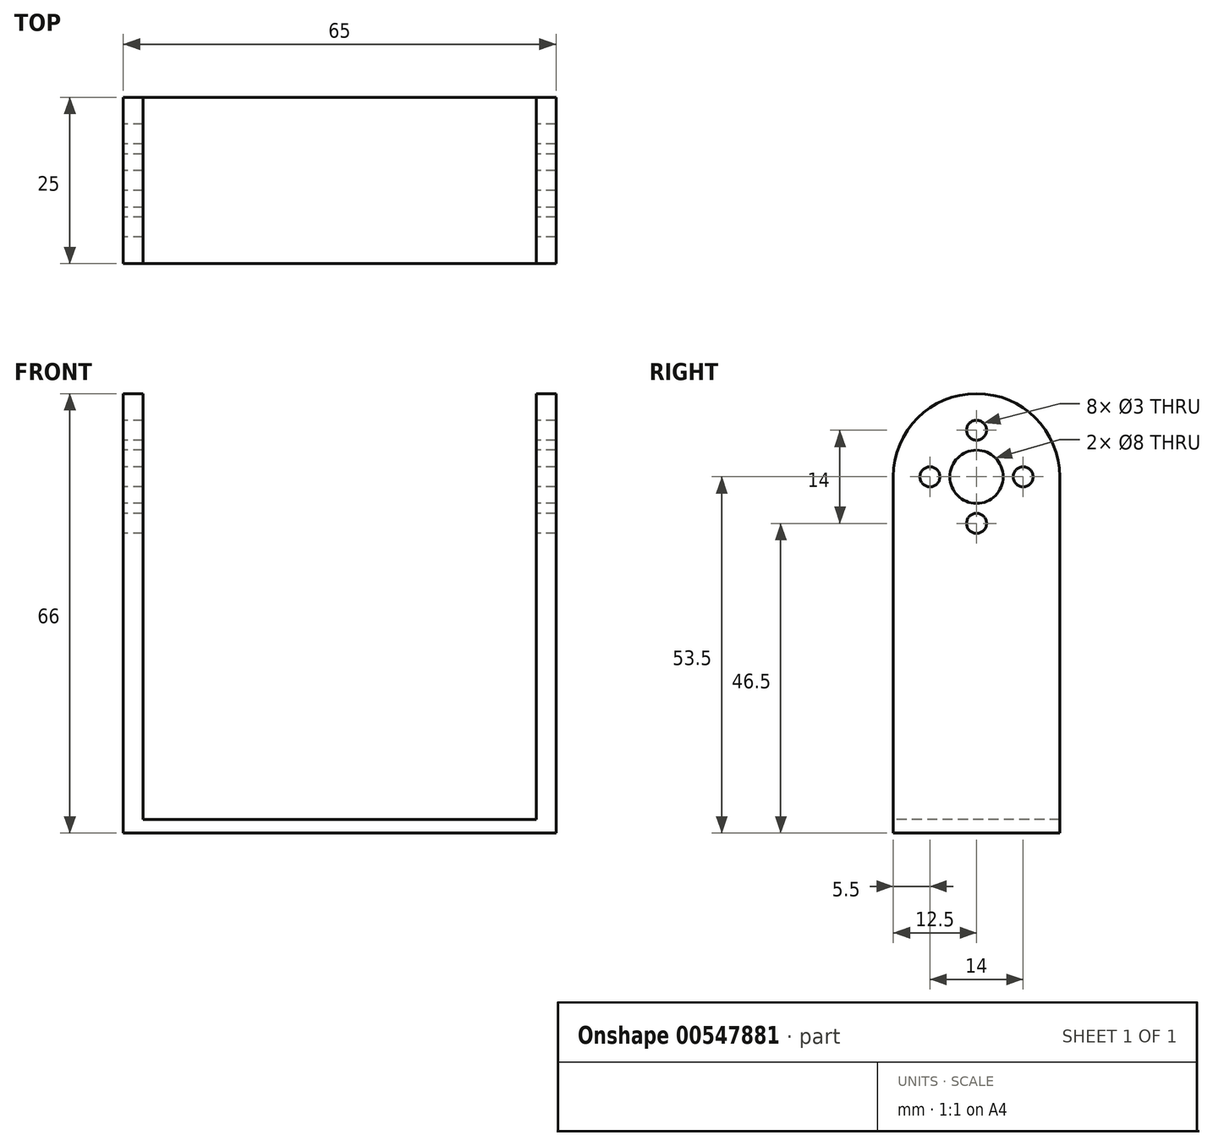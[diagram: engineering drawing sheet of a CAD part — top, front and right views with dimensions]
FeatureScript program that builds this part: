
annotation { "Feature Type Name" : "Feature", "Feature Type Description" : "" }
export const myFeature = defineFeature(function(context is Context, id is Id, definition is map)
    precondition{}
    {
        {
            var Q0;
            Q0=qCreatedBy(makeId("Top.planeOp"),FACE);
            var sketch = newSketch(context, id + "F0", { "sketchPlane" : qUnion([Q0])});
            skLineSegment(sketch, "E0.bottom", {"start": v(0, 0) * mm, "end": v(65, 0) * mm});
            skLineSegment(sketch, "E0.top", {"start": v(0, 25) * mm, "end": v(65, 25) * mm});
            skLineSegment(sketch, "E0.left", {"start": v(0, 0) * mm, "end": v(0, 25) * mm});
            skLineSegment(sketch, "E0.right", {"start": v(65, 0) * mm, "end": v(65, 25) * mm});
            skPoint(sketch, "E1.centerSnap0", {"position": v(0, 12.5) * mm});
            skPoint(sketch, "E1.centerSnap1", {"position": v(32.5, 0) * mm});
            skSolve(sketch);
        }
        {
            var Q0;
            Q0 = qSketchRegion(id + "F0", true);
            extrude(context, id + "F1", {"entities" : qUnion([Q0]), "depth" : 2 * mm, "offsetDistance" : 25 * mm});
        }
        {
            var Q0;
            Q0=qCreatedBy(makeId("Top.planeOp"),FACE);
            var sketch = newSketch(context, id + "F2", { "sketchPlane" : qUnion([Q0])});
            skLineSegment(sketch, "E2.bottom", {"start": v(0, 0) * mm, "end": v(3, 0) * mm});
            skLineSegment(sketch, "E2.top", {"start": v(0, 25) * mm, "end": v(3, 25) * mm});
            skLineSegment(sketch, "E2.left", {"start": v(0, 0) * mm, "end": v(0, 25) * mm});
            skLineSegment(sketch, "E2.right", {"start": v(3, 0) * mm, "end": v(3, 25) * mm});
            skLineSegment(sketch, "E3.bottom", {"start": v(62, 0) * mm, "end": v(65, 0) * mm});
            skLineSegment(sketch, "E3.top", {"start": v(62, 25) * mm, "end": v(65, 25) * mm});
            skLineSegment(sketch, "E3.left", {"start": v(62, 0) * mm, "end": v(62, 25) * mm});
            skLineSegment(sketch, "E3.right", {"start": v(65, 0) * mm, "end": v(65, 25) * mm});
            skSolve(sketch);
        }
        {
            var Q0;
            Q0 = qSketchRegion(id + "F2", true);
            extrude(context, id + "F3", {"entities" : qUnion([Q0]), "operationType" : NewBodyOperationType.ADD, "depth" : 66 * mm, "offsetDistance" : 25 * mm});
        }
        {
            var Q0;
            Q0=makeQuery(id+"F3.boolean.opBoolean","MERGE",FACE,{"derivedFrom":[makeQuery(id+"F1.opExtrude","SWEPT_FACE",FACE,{"disambiguationData":[OSD([sQuery(id+"F0.wireOp",EDGE,"E0.left")])]}),makeQuery(id+"F3.opExtrude","SWEPT_FACE",FACE,{"disambiguationData":[OSD([sQuery(id+"F2.wireOp",EDGE,"E2.left")])]})]});
            var sketch = newSketch(context, id + "F4", { "sketchPlane" : qUnion([Q0])});
            skArc(sketch, "E4", {"start": v(0, 53.5) * mm, "mid": v(-12.5, 66) * mm, "end": v(-25, 53.5) * mm});
            skPoint(sketch, "E4.centerSnap0", {"position": v(-12.5, 66) * mm});
            skLineSegment(sketch, "E5", {"start": v(-25, 53.5) * mm, "end": v(-25, 66) * mm});
            skLineSegment(sketch, "E6", {"start": v(-25, 66) * mm, "end": v(0, 66) * mm});
            skLineSegment(sketch, "E7", {"start": v(0, 66) * mm, "end": v(0, 53.5) * mm});
            skCircle(sketch, "E8", {"center": v(-12.5, 53.5) * mm, "radius": 4 * mm});
            skCircle(sketch, "E9", {"center": v(-12.5, 60.5) * mm, "radius": 1.5 * mm});
            skCircle(sketch, "E10.1.0", {"center": v(-19.5, 53.5) * mm, "radius": 1.5 * mm});
            skCircle(sketch, "E10.2.0", {"center": v(-12.5, 46.5) * mm, "radius": 1.5 * mm});
            skCircle(sketch, "E10.3.0", {"center": v(-5.5, 53.5) * mm, "radius": 1.5 * mm});
            skSolve(sketch);
        }
        {
            var Q0;
            Q0 = qSketchRegion(id + "F4", true);
            extrude(context, id + "F5", {"entities" : qUnion([Q0]), "operationType" : NewBodyOperationType.REMOVE, "endBound" : BoundingType.THROUGH_ALL, "oppositeDirection" : true, "depth" : 25 * mm, "offsetDistance" : 25 * mm});
        }
    });
